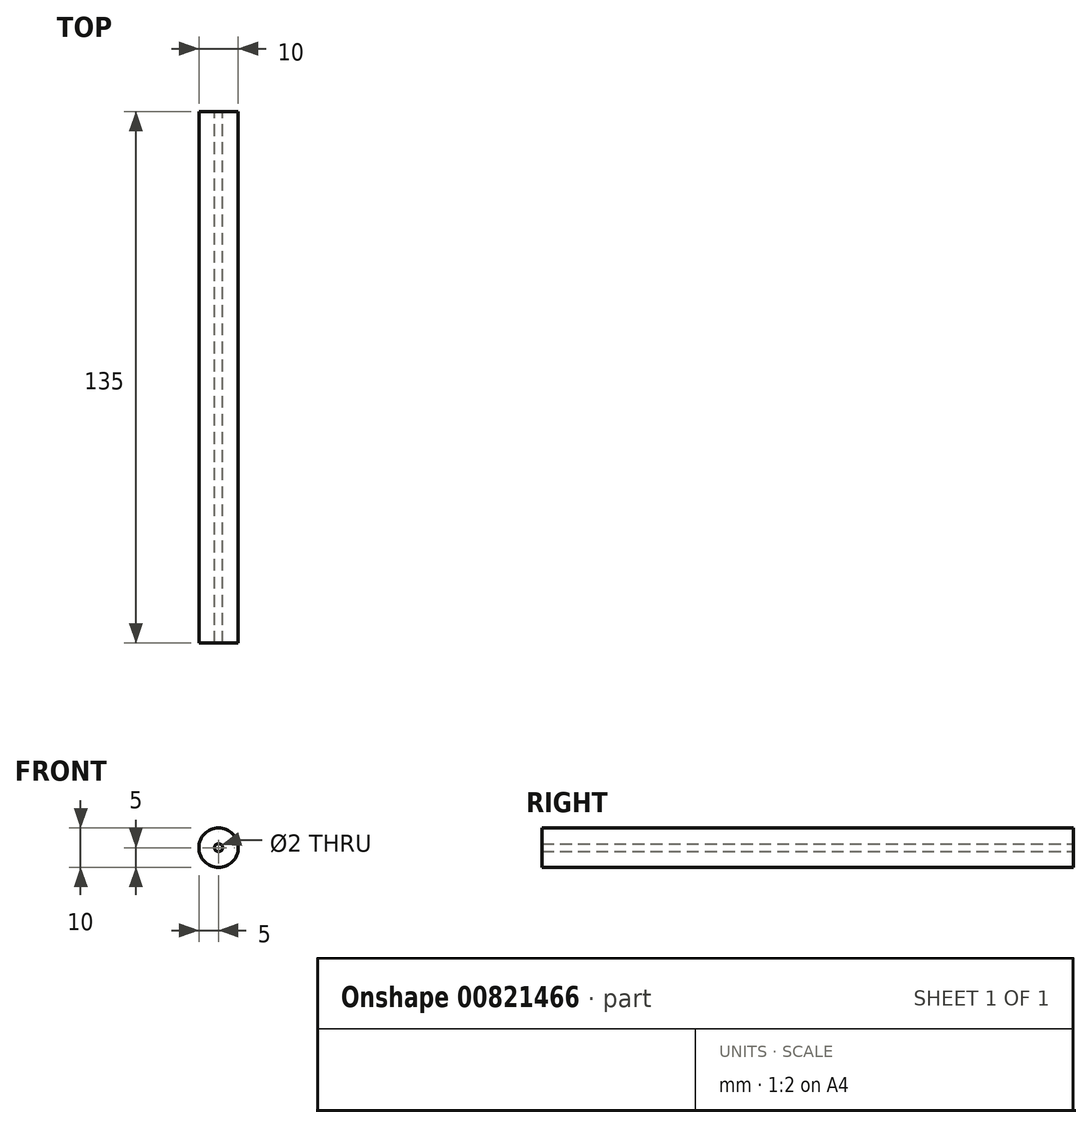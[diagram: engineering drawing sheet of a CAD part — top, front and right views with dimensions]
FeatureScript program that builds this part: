
annotation { "Feature Type Name" : "Feature", "Feature Type Description" : "" }
export const myFeature = defineFeature(function(context is Context, id is Id, definition is map)
    precondition{}
    {
        {
            var Q0;
            Q0=qCreatedBy(makeId("Front.planeOp"),FACE);
            var sketch = newSketch(context, id + "F0", { "sketchPlane" : qUnion([Q0])});
            skCircle(sketch, "E0", {"center": v(0, 0) * mm, "radius": 5 * mm});
            skSolve(sketch);
        }
        {
            var Q0;
            Q0=makeQuery(id+"F0.imprint","IMPRINT",FACE,{"disambiguationData":[TD([[makeQuery(id+"F0.imprint","IMPRINT",EDGE,{"derivedFrom":sQuery(id+"F0.wireOp",EDGE,"E0")}),1.0]])]});
            extrude(context, id + "F1", {"entities" : qUnion([Q0]), "depth" : 135 * mm, "offsetDistance" : 25.4 * mm});
        }
        {
            var Q0;
            Q0=qCreatedBy(makeId("Front.planeOp"),FACE);
            var sketch = newSketch(context, id + "F2", { "sketchPlane" : qUnion([Q0])});
            skCircle(sketch, "E1", {"center": v(0, 0) * mm, "radius": 1 * mm});
            skSolve(sketch);
        }
        {
            var Q0;
            Q0 = qSketchRegion(id + "F2", true);
            extrude(context, id + "F3", {"entities" : qUnion([Q0]), "operationType" : NewBodyOperationType.REMOVE, "endBound" : BoundingType.THROUGH_ALL, "depth" : 25.4 * mm, "offsetDistance" : 25.4 * mm});
        }
    });
